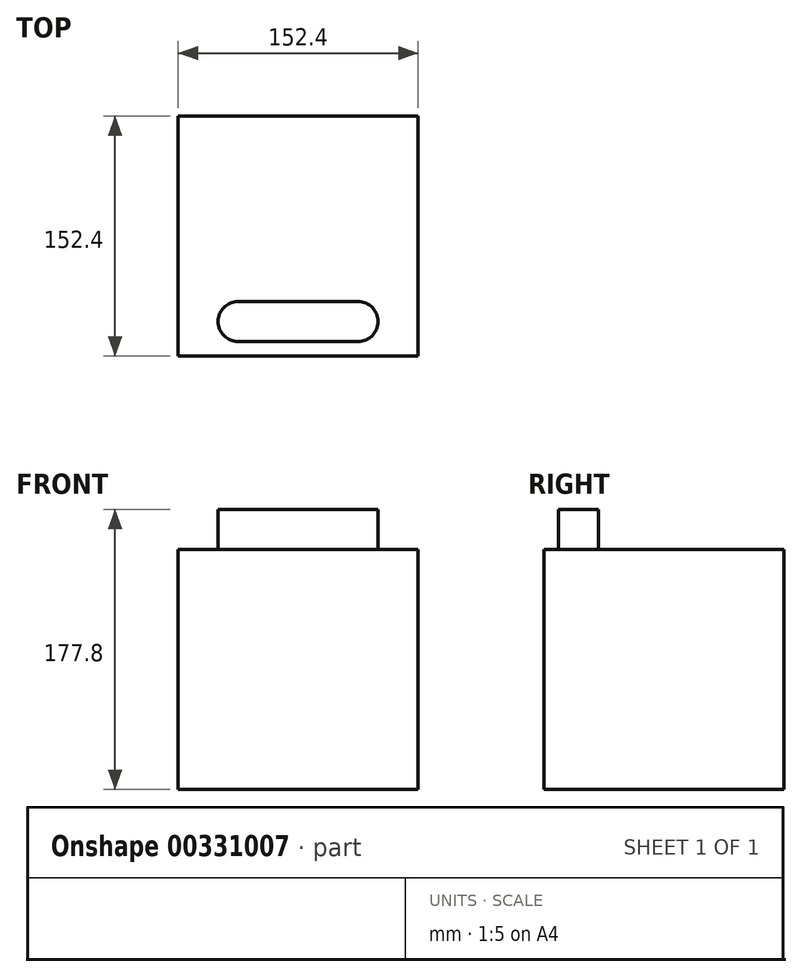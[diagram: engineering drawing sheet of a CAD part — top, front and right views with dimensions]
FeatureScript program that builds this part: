
annotation { "Feature Type Name" : "Feature", "Feature Type Description" : "" }
export const myFeature = defineFeature(function(context is Context, id is Id, definition is map)
    precondition{}
    {
        {
            var Q0;
            Q0=qCreatedBy(makeId("Top.planeOp"),FACE);
            var sketch = newSketch(context, id + "F0", { "sketchPlane" : qUnion([Q0])});
            skLineSegment(sketch, "E0.bottom", {"start": v(-76.22, 76.1) * mm, "end": v(76.18, 76.1) * mm});
            skLineSegment(sketch, "E0.top", {"start": v(-76.22, -76.3) * mm, "end": v(76.18, -76.3) * mm});
            skLineSegment(sketch, "E0.left", {"start": v(-76.22, 76.1) * mm, "end": v(-76.22, -76.3) * mm});
            skLineSegment(sketch, "E0.right", {"start": v(76.18, 76.1) * mm, "end": v(76.18, -76.3) * mm});
            skSolve(sketch);
        }
        {
            var Q0;
            Q0=makeQuery(id+"F0.imprint","IMPRINT",FACE,{"disambiguationData":[TD([[makeQuery(id+"F0.imprint","IMPRINT",EDGE,{"derivedFrom":sQuery(id+"F0.wireOp",EDGE,"E0.bottom")}),-1.0]])]});
            extrude(context, id + "F1", {"entities" : qUnion([Q0]), "depth" : 152.4 * mm});
        }
        {
            var Q0;
            Q0=makeQuery(id+"F1.opExtrude","CAP_FACE",FACE,{"disambiguationData":[OSD([sQuery(id+"F0.wireOp",EDGE,"E0.bottom"),sQuery(id+"F0.wireOp",EDGE,"E0.top"),sQuery(id+"F0.wireOp",EDGE,"E0.left"),sQuery(id+"F0.wireOp",EDGE,"E0.right")])],"isStart":false});
            var sketch = newSketch(context, id + "F2", { "sketchPlane" : qUnion([Q0])});
            skLineSegment(sketch, "E1", {"start": v(-76.22, -76.3) * mm, "end": v(-76.22, -54.4) * mm});
            skLineSegment(sketch, "E2", {"start": v(-76.22, -54.4) * mm, "end": v(76.18, -54.4) * mm});
            skSolve(sketch);
        }
        {
            var Q0;
            {var subQ0=sQuery(id+"F2.wireOp",EDGE,"E2");Q0=makeQuery(id+"F2.imprint","IMPRINT",FACE,{"disambiguationData":[TD([[makeQuery(id+"F2.imprint","IMPRINT",EDGE,{"derivedFrom":subQ0}),1.0]])]});}
            var sketch = newSketch(context, id + "F3", { "sketchPlane" : qUnion([Q0])});
            skLineSegment(sketch, "E3.0", {"start": v(-38.12, -67.1) * mm, "end": v(38.08, -67.1) * mm});
            skLineSegment(sketch, "E4.0", {"start": v(-38.12, -41.7) * mm, "end": v(38.08, -41.7) * mm});
            skLineSegment(sketch, "E5", {"start": v(-38.12, -41.7) * mm, "end": v(-38.12, -67.1) * mm});
            skLineSegment(sketch, "E6.0", {"start": v(38.08, -41.7) * mm, "end": v(38.08, -67.1) * mm});
            skArc(sketch, "E7", {"start": v(-38.12, -41.7) * mm, "mid": v(-50.82, -54.4) * mm, "end": v(-38.12, -67.1) * mm});
            skArc(sketch, "E8", {"start": v(38.08, -67.1) * mm, "mid": v(50.78, -54.4) * mm, "end": v(38.08, -41.7) * mm});
            skSolve(sketch);
        }
        {
            var Q0;
            Q0 = qSketchRegion(id + "F3", true);
            var Q1;
            Q1 = qSketchRegion(id + "F2", true);
            extrude(context, id + "F4", {"entities" : qUnion([Q0, Q1]), "operationType" : NewBodyOperationType.ADD, "depth" : 25.4 * mm});
        }
    });
